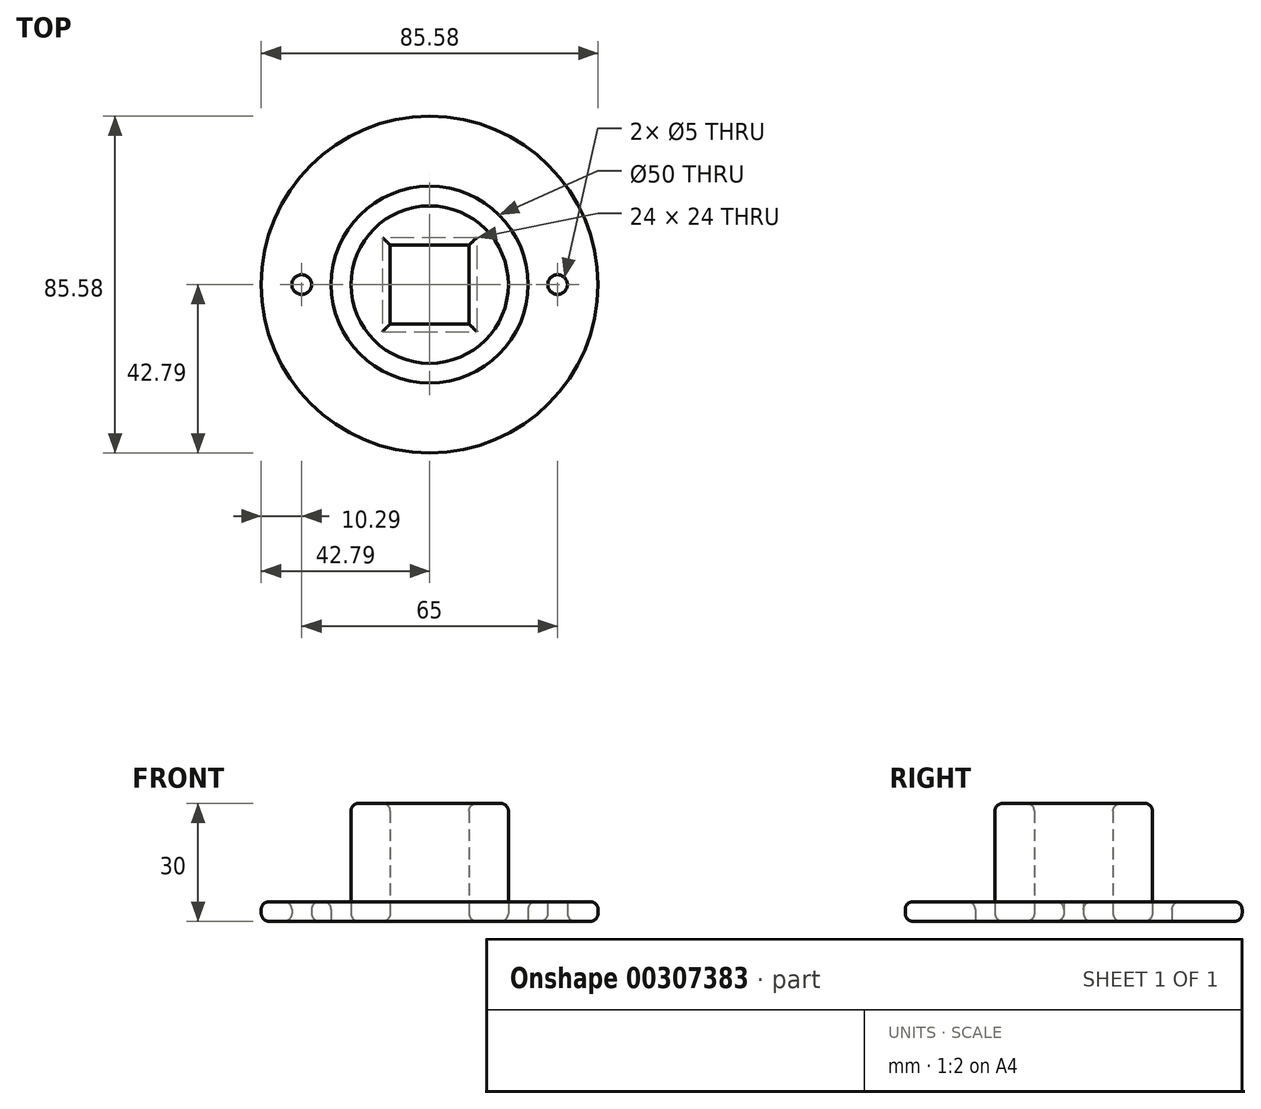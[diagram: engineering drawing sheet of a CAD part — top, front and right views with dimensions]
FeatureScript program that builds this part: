
annotation { "Feature Type Name" : "Feature", "Feature Type Description" : "" }
export const myFeature = defineFeature(function(context is Context, id is Id, definition is map)
    precondition{}
    {
        {
            var Q0;
            Q0=qCreatedBy(makeId("Top.planeOp"),FACE);
            var sketch = newSketch(context, id + "F0", { "sketchPlane" : qUnion([Q0])});
            skCircle(sketch, "E0", {"center": v(0, 0) * mm, "radius": 25 * mm});
            skCircle(sketch, "E1", {"center": v(0, 0) * mm, "radius": 32.5 * mm, "construction": true});
            skCircle(sketch, "E2", {"center": v(0, 0) * mm, "radius": 42.8 * mm});
            skCircle(sketch, "E3", {"center": v(0, 0) * mm, "radius": 20 * mm});
            skCircle(sketch, "E4", {"center": v(-32.5, 0) * mm, "radius": 2.5 * mm});
            skCircle(sketch, "E5", {"center": v(32.5, 0) * mm, "radius": 2.5 * mm});
            skLineSegment(sketch, "E6.bottom", {"start": v(-10, -10) * mm, "end": v(10, -10) * mm});
            skLineSegment(sketch, "E6.top", {"start": v(-10, 10) * mm, "end": v(10, 10) * mm});
            skLineSegment(sketch, "E6.left", {"start": v(-10, -10) * mm, "end": v(-10, 10) * mm});
            skLineSegment(sketch, "E6.right", {"start": v(10, -10) * mm, "end": v(10, 10) * mm});
            skSolve(sketch);
        }
        {
            var Q0;
            Q0 = qSketchRegion(id + "F0", true);
            extrude(context, id + "F1", {"entities" : qUnion([Q0]), "depth" : 5 * mm});
        }
        {
            var Q0;
            Q0=makeQuery(id+"F0.imprint","IMPRINT",FACE,{"disambiguationData":[TD([[makeQuery(id+"F0.imprint","IMPRINT",EDGE,{"derivedFrom":sQuery(id+"F0.wireOp",EDGE,"E3")}),1.0]])]});
            extrude(context, id + "F2", {"entities" : qUnion([Q0]), "depth" : 30 * mm});
        }
        {
            var Q0;
            Q0=makeQuery(id+"F1.opExtrude","CAP_EDGE",EDGE,{"disambiguationData":[OSD([sQuery(id+"F0.wireOp",EDGE,"E2")])],"isStart":true});
            var Q1;
            Q1=makeQuery(id+"F1.opExtrude","CAP_EDGE",EDGE,{"disambiguationData":[OSD([sQuery(id+"F0.wireOp",EDGE,"E2")])],"isStart":false});
            var Q2;
            Q2=makeQuery(id+"F1.opExtrude","CAP_EDGE",EDGE,{"disambiguationData":[OSD([sQuery(id+"F0.wireOp",EDGE,"E0")])],"isStart":false});
            var Q3;
            Q3=makeQuery(id+"F1.opExtrude","CAP_EDGE",EDGE,{"disambiguationData":[OSD([sQuery(id+"F0.wireOp",EDGE,"E4")])],"isStart":false});
            var Q4;
            Q4=makeQuery(id+"F2.opExtrude","CAP_EDGE",EDGE,{"disambiguationData":[OSD([sQuery(id+"F0.wireOp",EDGE,"E3")])],"isStart":false});
            var Q5;
            Q5=makeQuery(id+"F2.opExtrude","CAP_EDGE",EDGE,{"disambiguationData":[OSD([sQuery(id+"F0.wireOp",EDGE,"E3")])],"isStart":true});
            var Q6;
            Q6=makeQuery(id+"F2.opExtrude","CAP_EDGE",EDGE,{"disambiguationData":[OSD([sQuery(id+"F0.wireOp",EDGE,"E6.top")])],"isStart":false});
            var Q7;
            Q7=makeQuery(id+"F2.opExtrude","CAP_EDGE",EDGE,{"disambiguationData":[OSD([sQuery(id+"F0.wireOp",EDGE,"E6.left")])],"isStart":false});
            var Q8;
            Q8=makeQuery(id+"F2.opExtrude","CAP_EDGE",EDGE,{"disambiguationData":[OSD([sQuery(id+"F0.wireOp",EDGE,"E6.bottom")])],"isStart":false});
            var Q9;
            Q9=makeQuery(id+"F2.opExtrude","CAP_EDGE",EDGE,{"disambiguationData":[OSD([sQuery(id+"F0.wireOp",EDGE,"E6.right")])],"isStart":false});
            var Q10;
            Q10=makeQuery(id+"F2.opExtrude","CAP_EDGE",EDGE,{"disambiguationData":[OSD([sQuery(id+"F0.wireOp",EDGE,"E6.top")])],"isStart":true});
            var Q11;
            Q11=makeQuery(id+"F2.opExtrude","CAP_EDGE",EDGE,{"disambiguationData":[OSD([sQuery(id+"F0.wireOp",EDGE,"E6.right")])],"isStart":true});
            var Q12;
            Q12=makeQuery(id+"F2.opExtrude","CAP_EDGE",EDGE,{"disambiguationData":[OSD([sQuery(id+"F0.wireOp",EDGE,"E6.left")])],"isStart":true});
            var Q13;
            Q13=makeQuery(id+"F2.opExtrude","CAP_EDGE",EDGE,{"disambiguationData":[OSD([sQuery(id+"F0.wireOp",EDGE,"E6.bottom")])],"isStart":true});
            var Q14;
            Q14=makeQuery(id+"F1.opExtrude","CAP_EDGE",EDGE,{"disambiguationData":[OSD([sQuery(id+"F0.wireOp",EDGE,"E4")])],"isStart":true});
            var Q15;
            Q15=makeQuery(id+"F1.opExtrude","CAP_EDGE",EDGE,{"disambiguationData":[OSD([sQuery(id+"F0.wireOp",EDGE,"E5")])],"isStart":true});
            fillet(context, id + "F3", {"entities" : qUnion([Q0, Q1, Q2, Q3, Q4, Q5, Q6, Q7, Q8, Q9, Q10, Q11, Q12, Q13, Q14, Q15]), "radius" : 2 * mm, "tangentPropagation" : true, "allowEdgeOverflow" : false});
        }
    });
